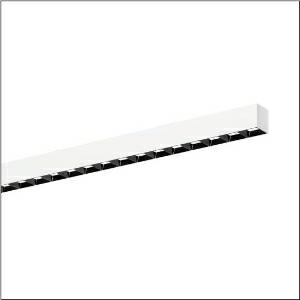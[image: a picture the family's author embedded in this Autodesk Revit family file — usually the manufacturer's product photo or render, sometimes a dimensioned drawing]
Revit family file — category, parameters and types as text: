
# Revit family: silica_r__21_51mx21dc3awb_ae09
name_source: partatom
category: Lighting Fixtures
units: mm (PartAtom-declared; Revit-internal decimal feet)

## family parameters
Cut with Voids When Loaded = No
Host = Face
Light Source = No
Part Type = Normal
Room Calculation Point = No
Round Connector Dimension = Use Diameter
Shared = No

## types (1)
- --- (1 x LED, 10800 lm, 69.3 W, 3000K)
    Apparent Load = 69 VA
    CIE Flux Codes = 87 99 100 100 100
    Color Rendering = 80
    Color Temperature = 3000K
    Default Elevation = 1800 mm
    Description = Silica® 21, office luminaire, primary light control with darklight reflector, of PMMA, black, CAT 2 (L<= 3000cd/m²), light emission: direct distribution, primary light characteristic: symmetric, installation type: surface-mounted, LED, rated luminous flux: 10.800lm, luminous efficacy: 156lm/W, light colour: 830, colour temperature: 3000K, control gear: DALI 2, with terminal, 3+2-pole, max. 2.5mm², mains connection: 220..240V, AC, 50/60Hz, luminaire housing, of aluminium, traffic white (RAL 9016), length: 3.004mm, width: 53mm, height: 53mm, protection rating (complete): IP20, insulation class (complete): insulation class I (protective earthing), certification: CE, permissible operating ambient temperature: 0..+35°C, standard: EN 50419, packaging unit: 1 piece
    Height = 53 mm
    Lamp = 1 x LED
    Lamp Light Flux = 10800 lm
    Lamp Power = 69.3 W
    Lamp count = 1
    Length = 3004 mm
    Luminous efficacy = 156 lm/W
    Manufacturer = Siteco
    ModVariant = No
    Model = 51MX21DC3AWB
    Mounting Place = Ceiling
    Mounting Type = Surface mounted
    Number of Poles = 1
    OnlyDefault = Yes
    Power Factor = 1
    Product Name = Silica® 21
    Product group = office luminaire | ceiling mounted
    ProductGroupID = 302
    Protection Class = Protection class I
    Protection Degree = IP 20
    RLX_Detail_Level = 1
    RLX_Emergency_Light_Flux = 0 lm
    RLX_Emergency_Type = 0
    RLX_Emergency_Type_DB = No
    RlxData = <blob elided: 63585 chars, md5=81af3174>
    Socket = socket
    Standby Power = 0 W
    System Light Flux = 10800 lm
    System Power = 69 W
    Type Comments = factory setting: luminous flux: 100 % | dim-lin: 254 | 393 mA
    Type Image = l_1335873.jpg
    URL = http://relux.com
    VarID = @adj_123832
    Voltage = 0 V
    Weight = 0.00 kg
    Width = 53 mm

## geometry (parser evidence)
native form markers: Blend x4, Sweep x11
no freeform markers — native parametric forms only
